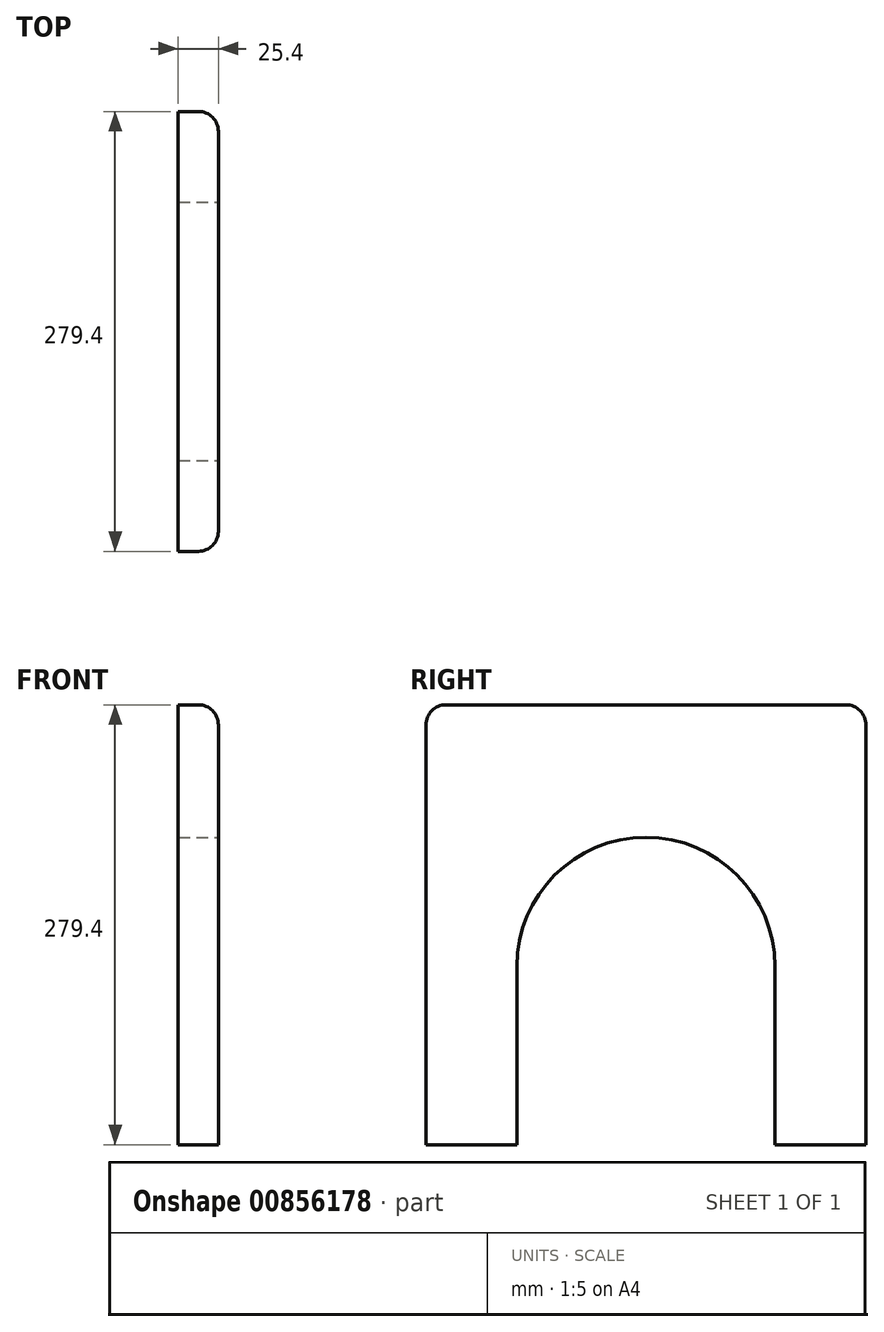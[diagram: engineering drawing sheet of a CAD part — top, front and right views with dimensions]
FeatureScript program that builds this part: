
annotation { "Feature Type Name" : "Feature", "Feature Type Description" : "" }
export const myFeature = defineFeature(function(context is Context, id is Id, definition is map)
    precondition{}
    {
        {
            var Q0;
            Q0=qCreatedBy(makeId("Right.planeOp"),FACE);
            var sketch = newSketch(context, id + "F0", { "sketchPlane" : qUnion([Q0])});
            skLineSegment(sketch, "E0.bottom", {"start": v(0, 0) * mm, "end": v(279.4, 0) * mm});
            skLineSegment(sketch, "E0.top", {"start": v(0, 279.4) * mm, "end": v(279.4, 279.4) * mm});
            skLineSegment(sketch, "E0.left", {"start": v(0, 0) * mm, "end": v(0, 279.4) * mm});
            skLineSegment(sketch, "E0.right", {"start": v(279.4, 0) * mm, "end": v(279.4, 279.4) * mm});
            skSolve(sketch);
        }
        {
            var Q0;
            Q0 = qSketchRegion(id + "F0", true);
            extrude(context, id + "F1", {"entities" : qUnion([Q0]), "depth" : 25.4 * mm, "offsetDistance" : 25.4 * mm});
        }
        {
            var Q0;
            Q0=makeQuery(id+"F1.opExtrude","CAP_FACE",FACE,{"disambiguationData":[OSD([sQuery(id+"F0.wireOp",EDGE,"E0.bottom"),sQuery(id+"F0.wireOp",EDGE,"E0.top"),sQuery(id+"F0.wireOp",EDGE,"E0.left"),sQuery(id+"F0.wireOp",EDGE,"E0.right")])],"isStart":false});
            var sketch = newSketch(context, id + "F2", { "sketchPlane" : qUnion([Q0])});
            skArc(sketch, "E1", {"start": v(221.64, 113.27) * mm, "mid": v(139.7, 195.2) * mm, "end": v(57.76, 113.27) * mm});
            skLineSegment(sketch, "E2.top", {"start": v(57.76, -113.27) * mm, "end": v(221.64, -113.27) * mm});
            skLineSegment(sketch, "E2.left", {"start": v(57.76, 113.27) * mm, "end": v(57.76, -113.27) * mm});
            skLineSegment(sketch, "E2.right", {"start": v(221.64, 113.27) * mm, "end": v(221.64, -113.27) * mm});
            skPoint(sketch, "E2.middle", {"position": v(139.7, 0) * mm});
            skSolve(sketch);
        }
        {
            var Q0;
            Q0 = qSketchRegion(id + "F2", true);
            extrude(context, id + "F3", {"entities" : qUnion([Q0]), "operationType" : NewBodyOperationType.REMOVE, "oppositeDirection" : true, "depth" : 25.4 * mm, "offsetDistance" : 25.4 * mm});
        }
        {
            var Q0;
            Q0=makeQuery(id+"F1.opExtrude","SWEPT_EDGE",EDGE,{"disambiguationData":[OSD([sQuery(id+"F0.wireOp",EDGE,"E0.top"),sQuery(id+"F0.wireOp",EDGE,"E0.left")])]});
            var Q1;
            Q1=makeQuery(id+"F1.opExtrude","SWEPT_EDGE",EDGE,{"disambiguationData":[OSD([sQuery(id+"F0.wireOp",EDGE,"E0.top"),sQuery(id+"F0.wireOp",EDGE,"E0.right")])]});
            fillet(context, id + "F4", {"entities" : qUnion([Q0, Q1]), "radius" : 12.7 * mm, "tangentPropagation" : true, "allowEdgeOverflow" : false});
        }
        {
            var Q0;
            Q0=makeQuery(id+"F1.opExtrude","CAP_EDGE",EDGE,{"disambiguationData":[OSD([sQuery(id+"F0.wireOp",EDGE,"E0.top")])],"isStart":false});
            fillet(context, id + "F5", {"entities" : qUnion([Q0]), "radius" : 12.7 * mm, "tangentPropagation" : true, "allowEdgeOverflow" : false});
        }
    });
